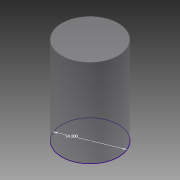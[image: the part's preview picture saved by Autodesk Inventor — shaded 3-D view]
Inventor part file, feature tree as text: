
AUTODESK INVENTOR PART (.ipt)
format: ipt  version: 2013 (Build 170138000, 138)  size: 72,704 bytes
history: native  units: in
note: dims shown in document units (in); Inventor stores cm internally (conversion verified against a paired STEP export)
features: extrude x1, sketch x1
ambient origin geometry x8: Origin, YZ Plane, XZ Plane, XY Plane, X Axis, Y Axis, Z Axis, Center Point
bodies: Solid1 (feature_tree)
feature tree (2):
  extrude  "Extrusion1"  Depth=84.0in TaperAngle=0.0deg
  sketch  "Sketch1"  dims[d0=54.0in d1=84.0in d2=0.0in]
